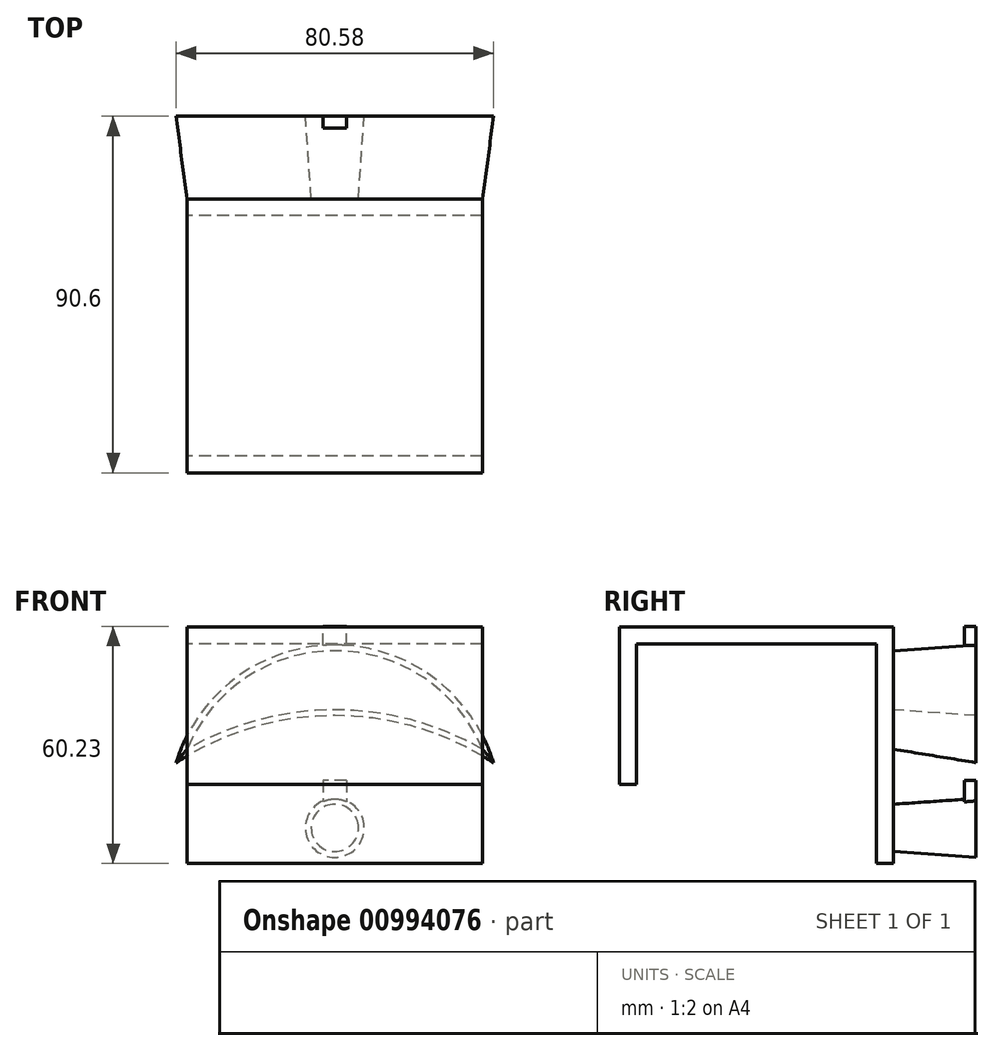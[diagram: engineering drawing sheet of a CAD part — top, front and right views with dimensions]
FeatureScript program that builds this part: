
annotation { "Feature Type Name" : "Feature", "Feature Type Description" : "" }
export const myFeature = defineFeature(function(context is Context, id is Id, definition is map)
    precondition{}
    {
        {
            var Q0;
            Q0=qCreatedBy(makeId("Right.planeOp"),FACE);
            var sketch = newSketch(context, id + "F0", { "sketchPlane" : qUnion([Q0])});
            skLineSegment(sketch, "E0.bottom", {"start": v(-69.6, 60) * mm, "end": v(-65.3, 60) * mm});
            skLineSegment(sketch, "E0.top", {"start": v(-69.6, 20) * mm, "end": v(-65.3, 20) * mm});
            skLineSegment(sketch, "E0.left", {"start": v(-69.6, 60) * mm, "end": v(-69.6, 20) * mm});
            skLineSegment(sketch, "E0.right", {"start": v(-65.3, 60) * mm, "end": v(-65.3, 20) * mm});
            skLineSegment(sketch, "E1.bottom", {"start": v(-65.3, 60) * mm, "end": v(0, 60) * mm});
            skLineSegment(sketch, "E1.top", {"start": v(-65.3, 55.7) * mm, "end": v(0, 55.7) * mm});
            skLineSegment(sketch, "E1.left", {"start": v(-65.3, 60) * mm, "end": v(-65.3, 55.7) * mm});
            skLineSegment(sketch, "E1.right", {"start": v(0, 60) * mm, "end": v(0, 55.7) * mm});
            skLineSegment(sketch, "E2.bottom", {"start": v(0, 55.7) * mm, "end": v(-4.3, 55.7) * mm});
            skLineSegment(sketch, "E2.top", {"start": v(0, 0) * mm, "end": v(-4.3, 0) * mm});
            skLineSegment(sketch, "E2.left", {"start": v(0, 55.7) * mm, "end": v(0, 0) * mm});
            skLineSegment(sketch, "E2.right", {"start": v(-4.3, 55.7) * mm, "end": v(-4.3, 0) * mm});
            skSolve(sketch);
        }
        {
            var Q0;
            Q0 = qSketchRegion(id + "F0", true);
            extrude(context, id + "F1", {"entities" : qUnion([Q0]), "depth" : 75 * mm, "offsetDistance" : 25 * mm});
        }
        {
            var Q0;
            Q0=makeQuery(id+"F1.opExtrude","SWEPT_FACE",FACE,{"disambiguationData":[OSD([sQuery(id+"F0.wireOp",EDGE,"E1.right"),sQuery(id+"F0.wireOp",EDGE,"E2.left")])]});
            var sketch = newSketch(context, id + "F2", { "sketchPlane" : qUnion([Q0])});
            skLineSegment(sketch, "E3", {"start": v(-37.5, 60) * mm, "end": v(-37.5, 54) * mm, "construction": true});
            skLineSegment(sketch, "E4", {"start": v(-37.5, 54) * mm, "end": v(-37.5, 29) * mm, "construction": true});
            skLineSegment(sketch, "E5", {"start": v(-37.5, 29) * mm, "end": v(-75, 29) * mm, "construction": true});
            skLineSegment(sketch, "E6", {"start": v(-37.5, 29) * mm, "end": v(0, 29) * mm, "construction": true});
            skArc(sketch, "E7", {"start": v(0, 29) * mm, "mid": v(-37.5, 54) * mm, "end": v(-75, 29) * mm});
            skArc(sketch, "E8", {"start": v(0, 29) * mm, "mid": v(-37.5, 39) * mm, "end": v(-75, 29) * mm});
            skLineSegment(sketch, "E9", {"start": v(-37.5, 39) * mm, "end": v(-37.5, 54) * mm, "construction": true});
            skLineSegment(sketch, "E10", {"start": v(-37.5, 29) * mm, "end": v(-37.5, 9) * mm, "construction": true});
            skCircle(sketch, "E11", {"center": v(-37.5, 9) * mm, "radius": 6 * mm});
            skSolve(sketch);
        }
        {
            var Q0;
            Q0=makeQuery(id+"F2.imprint","IMPRINT",FACE,{"disambiguationData":[TD([[makeQuery(id+"F2.imprint","IMPRINT",EDGE,{"derivedFrom":sQuery(id+"F2.wireOp",EDGE,"E7")}),1.0]])]});
            var Q1;
            Q1=makeQuery(id+"F2.imprint","IMPRINT",FACE,{"disambiguationData":[TD([[makeQuery(id+"F2.imprint","IMPRINT",EDGE,{"derivedFrom":sQuery(id+"F2.wireOp",EDGE,"E11")}),1.0]])]});
            extrude(context, id + "F3", {"entities" : qUnion([Q0, Q1]), "operationType" : NewBodyOperationType.ADD, "depth" : 21 * mm, "offsetDistance" : 25 * mm, "hasDraft" : true, "draftAngle" : 4 * degree});
        }
        {
            var Q0;
            Q0=makeQuery(id+"F3.opExtrude","CAP_FACE",FACE,{"disambiguationData":[OSD([sQuery(id+"F2.wireOp",EDGE,"E7"),sQuery(id+"F2.wireOp",EDGE,"E8")])],"isStart":false});
            var sketch = newSketch(context, id + "F4", { "sketchPlane" : qUnion([Q0])});
            skLineSegment(sketch, "E12.bottom", {"start": v(-40.48, 50.7) * mm, "end": v(-34.52, 50.7) * mm});
            skLineSegment(sketch, "E12.top", {"start": v(-40.48, 60.23) * mm, "end": v(-34.52, 60.23) * mm});
            skLineSegment(sketch, "E12.left", {"start": v(-40.48, 50.7) * mm, "end": v(-40.48, 60.23) * mm});
            skLineSegment(sketch, "E12.right", {"start": v(-34.52, 50.7) * mm, "end": v(-34.52, 60.23) * mm});
            skPoint(sketch, "E12.middle", {"position": v(-37.5, 55.47) * mm});
            skLineSegment(sketch, "E13.bottom", {"start": v(-40.48, 21.07) * mm, "end": v(-34.52, 21.07) * mm});
            skLineSegment(sketch, "E13.top", {"start": v(-40.48, 5.68) * mm, "end": v(-34.52, 5.68) * mm});
            skLineSegment(sketch, "E13.left", {"start": v(-40.48, 21.07) * mm, "end": v(-40.48, 5.68) * mm});
            skLineSegment(sketch, "E13.right", {"start": v(-34.52, 21.07) * mm, "end": v(-34.52, 5.68) * mm});
            skPoint(sketch, "E13.middle", {"position": v(-37.5, 13.37) * mm});
            skSolve(sketch);
        }
        {
            var Q0;
            {var subQ0=sQuery(id+"F4.wireOp",EDGE,"E12.top");Q0=makeQuery(id+"F4.imprint","IMPRINT",FACE,{"disambiguationData":[TD([[makeQuery(id+"F4.imprint","IMPRINT",EDGE,{"derivedFrom":subQ0}),-1.0]])]});}
            var Q1;
            Q1=makeQuery(id+"F4.imprint","IMPRINT",FACE,{"disambiguationData":[TD([[makeQuery(id+"F4.imprint","IMPRINT",EDGE,{"derivedFrom":sQuery(id+"F4.wireOp",EDGE,"E13.bottom")}),-1.0]])]});
            extrude(context, id + "F5", {"entities" : qUnion([Q0, Q1]), "operationType" : NewBodyOperationType.ADD, "oppositeDirection" : true, "depth" : 3 * mm, "offsetDistance" : 25 * mm});
        }
    });
